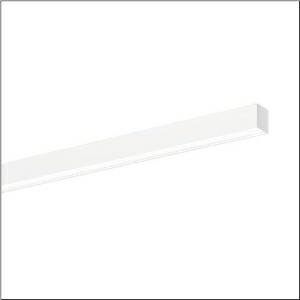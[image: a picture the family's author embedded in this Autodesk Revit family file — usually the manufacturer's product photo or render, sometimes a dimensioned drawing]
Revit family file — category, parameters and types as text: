
# Revit family: silica_r__21_51mx20dc45wb_dec1
name_source: partatom
category: Lighting Fixtures
units: mm (PartAtom-declared; Revit-internal decimal feet)

## family parameters
Cut with Voids When Loaded = No
Host = Face
Light Source = No
Part Type = Normal
Room Calculation Point = No
Round Connector Dimension = Use Diameter
Shared = No

## types (1)
- --- (1 x LED, 6000 lm, 40.1 W, 4000K)
    Apparent Load = 40 VA
    CIE Flux Codes = 48 79 96 100 100
    Color Rendering = 80
    Color Temperature = 4000K
    Default Elevation = 1800 mm
    Description = Silica® 21, office luminaire, primary optical cover: cover, of PMMA, opal, light emission: direct distribution, primary light characteristic: symmetric, installation type: surface-mounted, LED, rated luminous flux: 6.000lm, luminous efficacy: 150lm/W, light colour: 840, colour temperature: 4000K, control gear: DALI 2, with terminal, 3+2-pole, max. 2.5mm², mains connection: 220..240V, AC, 50/60Hz, rated input power: 40.1W, luminaire housing, of aluminium, traffic white (RAL 9016), length: 3.004mm, width: 53mm, height: 53mm, protection rating (complete): IP20, insulation class (complete): insulation class I (protective earthing), certification: CE, permissible operating ambient temperature: 0..+35°C, standard: EN 50419, packaging unit: 1 piece
    Height = 53 mm
    Lamp = 1 x LED
    Lamp Light Flux = 6000 lm
    Lamp Power = 40.1 W
    Lamp count = 1
    Length = 3004 mm
    Luminous efficacy = 150 lm/W
    Manufacturer = Siteco
    ModVariant = No
    Model = 51MX20DC45WB
    Mounting Place = Ceiling
    Mounting Type = Surface mounted
    Number of Poles = 1
    OnlyDefault = Yes
    Power Factor = 1
    Product Name = Silica® 21
    Product group = office luminaire | ceiling mounted
    ProductGroupID = 302
    Protection Class = Protection class I
    Protection Degree = IP 20
    RLX_Detail_Level = 1
    RLX_Emergency_Light_Flux = 0 lm
    RLX_Emergency_Type = 0
    RLX_Emergency_Type_DB = No
    RlxData = <blob elided: 23829 chars, md5=2ddeda04>
    Socket = socket
    Standby Power = 0 W
    System Light Flux = 6000 lm
    System Power = 40 W
    Type Comments = factory setting: luminous flux: 100 % | dim-lin: 254 | 218 mA
    Type Image = l_1335877.jpg
    URL = http://relux.com
    VarID = @adj_117886
    Voltage = 0 V
    Weight = 0.00 kg
    Width = 53 mm

## geometry (parser evidence)
native form markers: Blend x4, Sweep x12
no freeform markers — native parametric forms only
